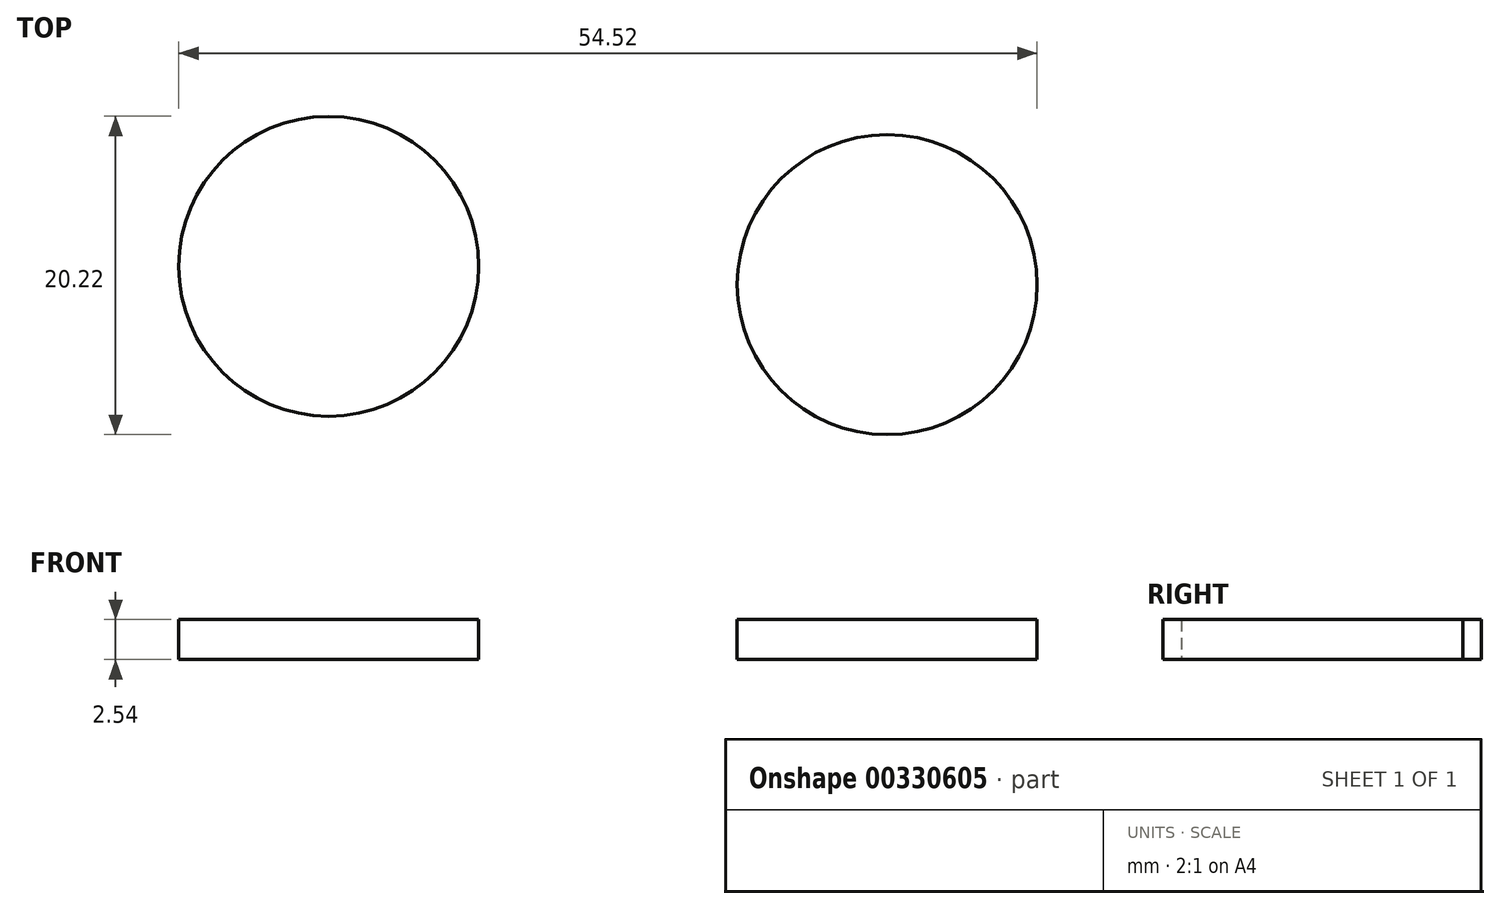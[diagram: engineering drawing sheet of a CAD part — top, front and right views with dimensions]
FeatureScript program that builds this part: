
annotation { "Feature Type Name" : "Feature", "Feature Type Description" : "" }
export const myFeature = defineFeature(function(context is Context, id is Id, definition is map)
    precondition{}
    {
        {
            var Q0;
            Q0=qCreatedBy(makeId("Top.planeOp"),FACE);
            var sketch = newSketch(context, id + "F0", { "sketchPlane" : qUnion([Q0])});
            skCircle(sketch, "E0", {"center": v(-36, 39.61) * mm, "radius": 9.52 * mm});
            skCircle(sketch, "E1", {"center": v(-0.53, 38.45) * mm, "radius": 9.53 * mm});
            skSolve(sketch);
        }
        {
            var Q0;
            Q0=makeQuery(id+"F0.imprint","IMPRINT",FACE,{"disambiguationData":[TD([[makeQuery(id+"F0.imprint","IMPRINT",EDGE,{"derivedFrom":sQuery(id+"F0.wireOp",EDGE,"E0")}),1.0]])]});
            var Q1;
            Q1=makeQuery(id+"F0.imprint","IMPRINT",FACE,{"disambiguationData":[TD([[makeQuery(id+"F0.imprint","IMPRINT",EDGE,{"derivedFrom":sQuery(id+"F0.wireOp",EDGE,"E1")}),1.0]])]});
            extrude(context, id + "F1", {"entities" : qUnion([Q0, Q1]), "depth" : 2.54 * mm});
        }
    });
